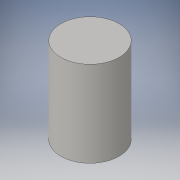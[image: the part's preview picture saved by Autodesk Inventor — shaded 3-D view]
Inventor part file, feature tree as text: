
AUTODESK INVENTOR PART (.ipt)
format: ipt  version: 2016 (Build 200138000, 138)  size: 83,968 bytes
history: native  units: in
note: dims shown in document units (in); Inventor stores cm internally (conversion verified against a paired STEP export)
features: sketch x2, extrude x1
ambient origin geometry x8: Origin, YZ Plane, XZ Plane, XY Plane, X Axis, Y Axis, Z Axis, Center Point
bodies: Solid1 (feature_tree)
feature tree (3):
  sketch  "Sketch1"  dims[d0=0.3937in d1=0.5787in d2=0.0in]
  extrude  "Extrusion1"  Depth=0.5787in TaperAngle=0.0deg
  sketch  "Sketch2"
